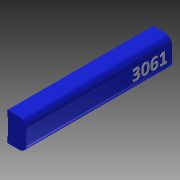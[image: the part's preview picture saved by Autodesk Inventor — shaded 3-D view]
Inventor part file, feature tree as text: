
AUTODESK INVENTOR PART (.ipt)
format: ipt  version: 2013 (Build 170138000, 138)  size: 302,080 bytes
history: native  units: in
note: dims shown in document units (in); Inventor stores cm internally (conversion verified against a paired STEP export)
features: extrude x4, reference x4, sketch x3, projected_geometry x1
ambient origin geometry x8: Origin, YZ Plane, XZ Plane, XY Plane, X Axis, Y Axis, Z Axis, Center Point
bodies: Solid1 (feature_tree)
feature tree (12):
  sketch  "Sketch1"  dims[d0=0.0625in d1=0.0in d3=1.0in]
  extrude  "Extrusion1"  Depth=1.0in
  extrude  "Extrusion2"  Depth=0.0625in
  extrude  "Extrusion3"  Depth=0.0625in TaperAngle=0.0deg
  extrude  "Extrusion5"  Depth=6.0in
  reference  "Reference4"
  reference  "Reference5"
  sketch  "Sketch2"  dims[d7=1.0in d9=0.0625in]
  sketch  "Sketch3"  dims[d10=25.875in d11=0.0in d12=0.0625in d13=0.0in d42=6.0in d43=0.0625in d44=0.0in d45=0.0625in d46=0.0625in d47=1.0in d48=2.5in]
  reference  "Reference6"
  projected_geometry  "Projected Loop1"
  reference  "Reference7"
